# Revit family: Power-ModularDevices-GEWISS-90AM-SPD_TYPE2_1PN
name_source: partatom
category: Apparecchi elettrici
revit_build: Autodesk Revit 2016 (Build: 20161004_0715(x64)
units: mm (PartAtom-declared; Revit-internal decimal feet)

## family parameters
Condiviso = No
Host = Superficie
Mantenere orientamento annotazione = Sì
Numero OmniClass = 23.80.50.00
Punto di calcolo locali = Sì
Quota connettore circolare = Usa diametro
Taglio con vuoti quando caricato = No
Tipo di parte = Normale
Titolo OmniClass = Terminals for Power Supply

## types (3) — shared parameters
Catalogue = POWER
Catalogue Range = 90 AM
Electrocod = 0642
IDF = 7729b77d-9e49-4fa8-a4b9-cbce93b88dd9
IDT = fe1e984c-5491-4d5b-93ee-6502594b4586
Immagine tipo = GWD6407.jpg
No. Chorus modules = 2
No. of modules EN 50022 = 2
No. of poles = 1P+N
Number of poles = 1P+N
Numero di poli = 1
Produttore = GEWISS S.p.A.
Prospetto di default = 1219 mm
Rated voltage = 230Vac
Rated voltage AC = 230V
SEO = Limiter
Spostamento_x = -340 mm
Technical sheet = https://www.gewiss.com
Type = 2
Type: = 2
URL = https://www.gewiss.com
Version file RFA = 18.0
carico = Altro
potenza in watt = 0 V

## per-type parameters (varying)
| type | Descrizione | EAN code | Maximum discharge current: | Modello |
| GWD6418 - LST - SPD 1P+N 40KA AUX. T2 | LST - SPD 1P+N 40KA AUX. T2 | 8011564774902 | 40KA | GWD6418 |
| GWD6407 - LST - SPD 1P+N 20KA T2 | LST - SPD 1P+N 20KA T2 | 8011564774841 | 20KA | GWD6407 |
| GWD6417 - LST - SPD 1P+N 40KA T2 | LST - SPD 1P+N 40KA T2 | 8011564774896 | 40KA | GWD6417 |
